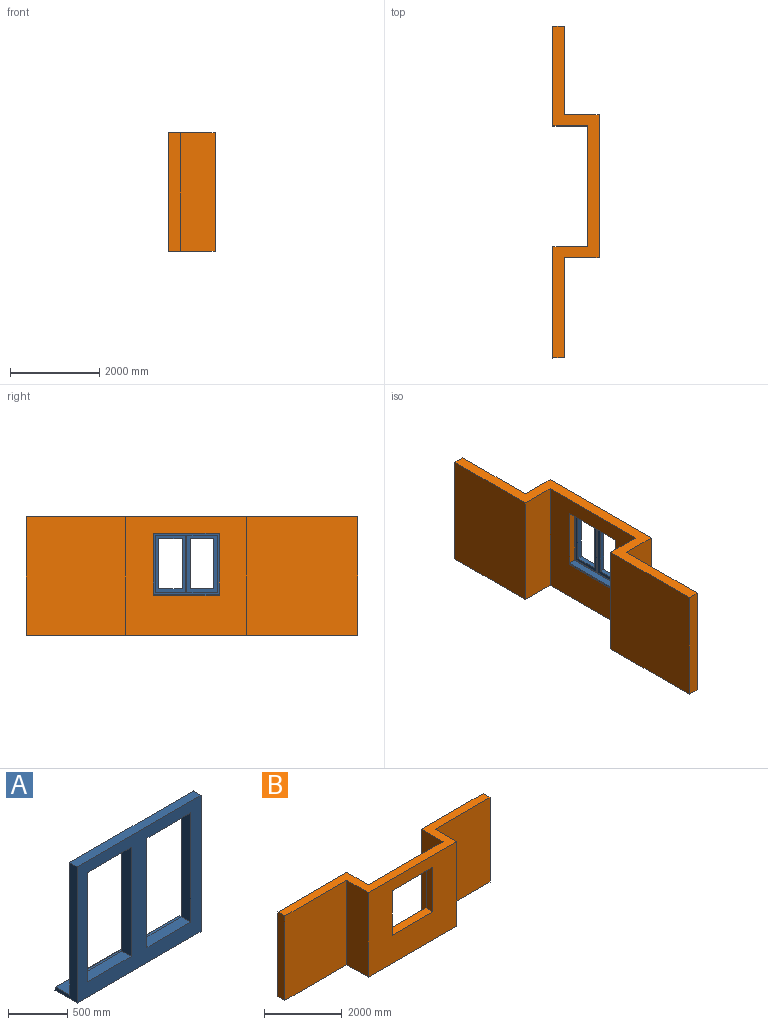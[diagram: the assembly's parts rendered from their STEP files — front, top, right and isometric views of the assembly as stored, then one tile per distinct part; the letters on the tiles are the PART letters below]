
ASSEMBLY  parts=2 mates=1
PART A: 27 faces, bbox 1474x263x1402 mm
  f0: plane 683x20mm, normal (0,0,-1), area 13660mm2, adj f1,f3,f8,f10
  f1: plane 1285x20mm, normal (-1,0,0), area 25700mm2, adj f0,f2,f8,f10
  f2: plane 683x20mm, normal (0,0,1), area 13660mm2, adj f1,f3,f8,f10
  f3: plane 1285x20mm, normal (1,0,0), area 25700mm2, adj f0,f2,f8,f10
  f4: plane 1285x20mm, normal (-1,0,0), area 25700mm2, adj f5,f7,f9,f10
  f5: plane 683x20mm, normal (0,0,1), area 13660mm2, adj f4,f6,f9,f10
  f6: plane 1285x20mm, normal (1,0,0), area 25700mm2, adj f5,f7,f9,f10
  f7: plane 683x20mm, normal (0,0,-1), area 13660mm2, adj f4,f6,f9,f10
  f8: plane 1285x683mm, normal (0,1,0), area 289280mm2, adj f0,f1,f2,f3,f14,f15,f16,f17
  f9: plane 1285x683mm, normal (0,1,0), area 289280mm2, adj f4,f5,f6,f7,f18,f19,f20,f21
  f10: plane 1474x1365mm, normal (0,1,0), area 256700mm2, adj f0,f1,f2,f3,f4,f5,f6,f7
  f11: cylinder r=6mm len=1474mm, axis (1,0,0), area 12704.2mm2, adj f12,f13,f22,f24
  f12: plane 1474x31.8mm, normal (0,0.99,0.13), area 47304.5mm2, adj f11,f22,f23,f24
  f13: plane 1474x162.76mm, normal (0,0,1), area 239903.6mm2, adj f10,f11,f22,f24
  f14: plane 1125x110mm, normal (1,0,0), area 123750mm2, adj f8,f15,f17,f25
  f15: plane 523x110mm, normal (0,0,-1), area 57530mm2, adj f8,f14,f16,f25
  f16: plane 1125x110mm, normal (-1,0,0), area 123750mm2, adj f8,f15,f17,f25
  f17: plane 523x110mm, normal (0,0,1), area 57530mm2, adj f8,f14,f16,f25
  f18: plane 1125x110mm, normal (1,0,0), area 123750mm2, adj f9,f19,f21,f25
  f19: plane 523x110mm, normal (0,0,-1), area 57530mm2, adj f9,f18,f20,f25
  f20: plane 1125x110mm, normal (-1,0,0), area 123750mm2, adj f9,f19,f21,f25
  f21: plane 523x110mm, normal (0,0,1), area 57530mm2, adj f9,f18,f20,f25
  f22: plane 1402x263mm, normal (-1,0,0), area 132484.6mm2, adj f10,f11,f12,f13,f23,f25,f26
  f23: plane 1474x263mm, normal (0,0,-1), area 387662mm2, adj f12,f22,f24,f25
  f24: plane 1402x263mm, normal (1,0,0), area 132482.9mm2, adj f10,f11,f12,f13,f23,f25,f26
  f25: plane 1474x1402mm, normal (0,-1,0), area 889798mm2, adj f14,f15,f16,f17,f18,f19,f20,f21
  f26: plane 1474x90mm, normal (0,0,1), area 132660mm2, adj f10,f22,f24,f25
PART B: 18 faces, bbox 7446x1035x2655 mm
  f0: plane 2655x2496mm, normal (0,1,0), area 6626880mm2, adj f1,f8,f9,f11
  f1: plane 2655x250mm, normal (-1,0,0), area 663750mm2, adj f0,f2,f8,f11
  f2: plane 2655x2246mm, normal (0,-1,0), area 5963130mm2, adj f1,f7,f8,f11
  f3: plane 2655x1990mm, normal (0,-1,0), area 5283450mm2, adj f4,f6,f8,f11
  f4: plane 2655x250mm, normal (1,0,0), area 663750mm2, adj f3,f5,f8,f11
  f5: plane 2655x2240mm, normal (0,1,0), area 5947200mm2, adj f4,f8,f11,f12
  f6: plane 2655x785mm, normal (1,0,0), area 2084175mm2, adj f3,f8,f10,f11
  f7: plane 2655x785mm, normal (-1,0,0), area 2084175mm2, adj f2,f8,f10,f11
  f8: plane 7446x1035mm, normal (0,0,1), area 2254000mm2, adj f0,f1,f2,f3,f4,f5,f6,f7
  f9: plane 2655x785mm, normal (1,0,0), area 2084175mm2, adj f0,f8,f11,f13
  f10: plane 3210x2655mm, normal (0,-1,0), area 6456002mm2, adj f6,f7,f8,f11,f14,f15,f16,f17
  f11: plane 7446x1035mm, normal (0,0,-1), area 2254000mm2, adj f0,f1,f2,f3,f4,f5,f6,f7
  f12: plane 2655x785mm, normal (-1,0,0), area 2084175mm2, adj f5,f8,f11,f13
  f13: plane 2710x2655mm, normal (0,1,0), area 5128502mm2, adj f8,f9,f11,f12,f14,f15,f16,f17
  f14: plane 1402x250mm, normal (1,0,0), area 350500mm2, adj f10,f13,f15,f17
  f15: plane 1474x250mm, normal (0,0,-1), area 368500mm2, adj f10,f13,f14,f16
  f16: plane 1402x250mm, normal (-1,0,0), area 350500mm2, adj f10,f13,f15,f17
  f17: plane 1474x250mm, normal (0,0,1), area 368500mm2, adj f10,f13,f14,f16
PLACE A rot(axis=(0,0,1),90deg) t=(2067.41,-2263.66,31.72)mm
PLACE B rot(axis=(0,0,1),90deg) t=(2067.41,-2263.66,31.72)mm
MATE fastened A.f25 <-> B.f10  axis (1,0,0) through (3102.41,850.34,914.72)mm
